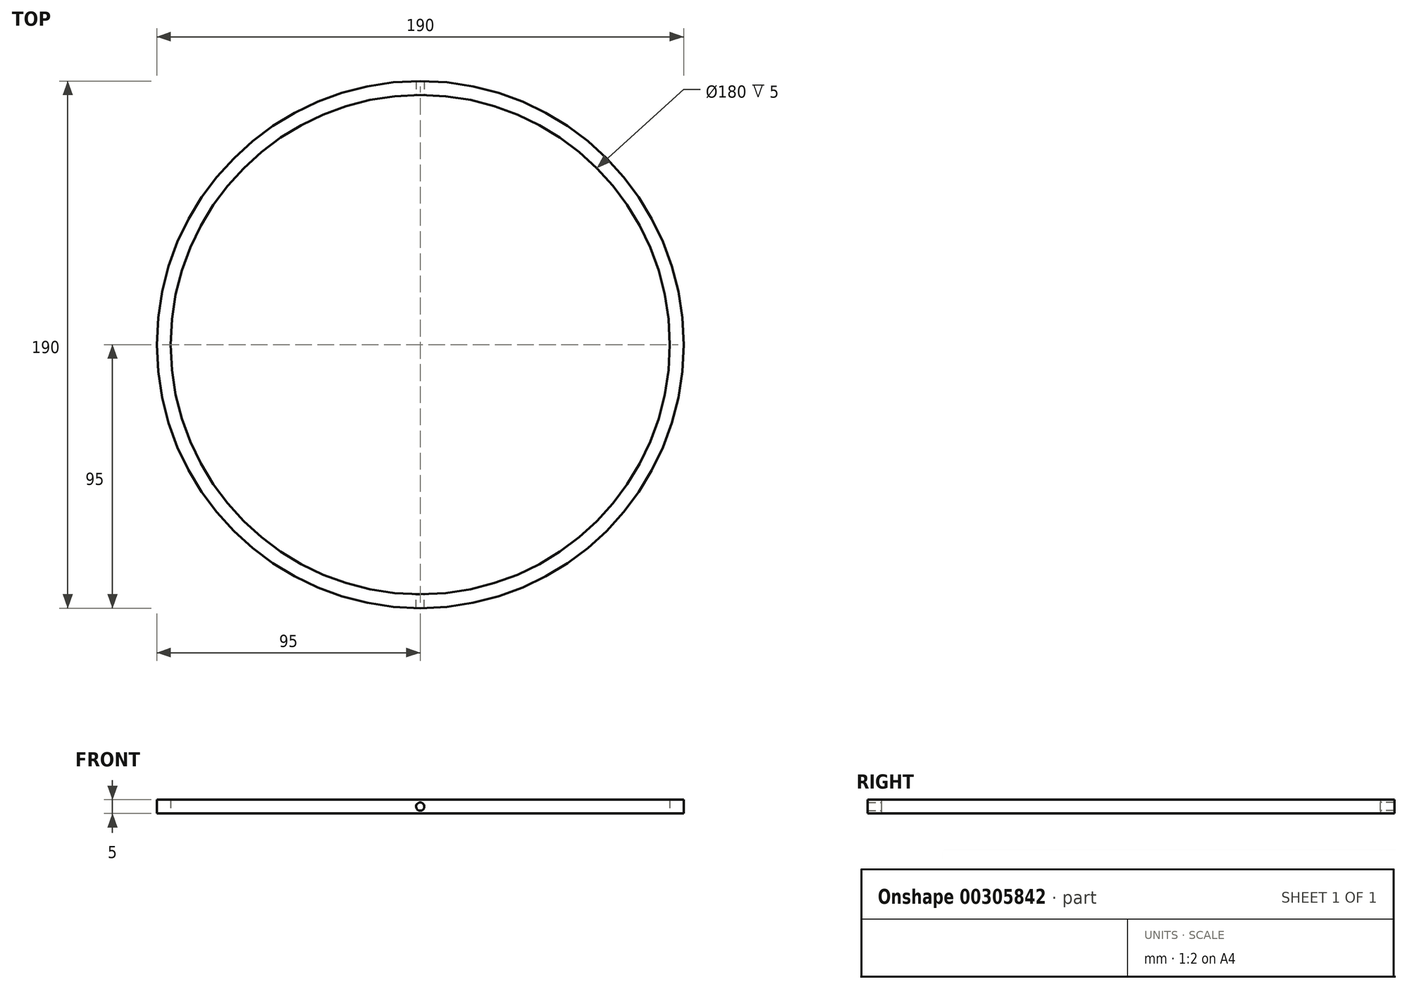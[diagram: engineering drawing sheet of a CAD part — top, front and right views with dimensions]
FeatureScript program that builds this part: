
annotation { "Feature Type Name" : "Feature", "Feature Type Description" : "" }
export const myFeature = defineFeature(function(context is Context, id is Id, definition is map)
    precondition{}
    {
        {
            var Q0;
            Q0=qCreatedBy(makeId("Front.planeOp"),FACE);
            var sketch = newSketch(context, id + "F0", { "sketchPlane" : qUnion([Q0])});
            skLineSegment(sketch, "E0.bottom", {"start": v(-95, 5) * mm, "end": v(-90, 5) * mm});
            skLineSegment(sketch, "E0.top", {"start": v(-95, 0) * mm, "end": v(-90, 0) * mm});
            skLineSegment(sketch, "E0.left", {"start": v(-95, 5) * mm, "end": v(-95, 0) * mm});
            skLineSegment(sketch, "E0.right", {"start": v(-90, 5) * mm, "end": v(-90, 0) * mm});
            skLineSegment(sketch, "E1", {"start": v(0, 0) * mm, "end": v(0, 2.5) * mm});
            skPoint(sketch, "E2", {"position": v(0, 2.5) * mm});
            skSolve(sketch);
        }
        {
            var Q0;
            Q0=makeQuery(id+"F0.imprint","IMPRINT",FACE,{"disambiguationData":[TD([[makeQuery(id+"F0.imprint","IMPRINT",EDGE,{"derivedFrom":sQuery(id+"F0.wireOp",EDGE,"E0.bottom")}),-1.0]])]});
            var Q1;
            Q1=sQuery(id+"F0.wireOp",EDGE,"E1");
            revolve(context, id + "F1", {"entities" : qUnion([Q0]), "axis" : qUnion([Q1]), "revolveType" : RevolveType.FULL});
        }
        {
            var Q0;
            Q0=sQuery(id+"F0.wireOp",VERTEX,"E2");
            var Q1;
            Q1=makeQuery(id+"F1.opRevolve","SWEPT_BODY",BODY,{"disambiguationData":[OSD([sQuery(id+"F0.wireOp",EDGE,"E0.bottom"),sQuery(id+"F0.wireOp",EDGE,"E0.top"),sQuery(id+"F0.wireOp",EDGE,"E0.left"),sQuery(id+"F0.wireOp",EDGE,"E0.right")])]});
            hole(context, id + "F2", {"style" : HoleStyle.SIMPLE, "endStyle" : HoleEndStyle.THROUGH, "holeDiameter" : 3 * mm, "tappedDepth" : 12 * mm, "tapClearance" : 3, "locations" : qUnion([Q0]), "scope" : qUnion([Q1])});
        }
        {
            var Q0;
            Q0=sQuery(id+"F0.wireOp",VERTEX,"E2");
            var Q1;
            Q1=makeQuery(id+"F1.opRevolve","SWEPT_BODY",BODY,{"disambiguationData":[OSD([sQuery(id+"F0.wireOp",EDGE,"E0.bottom"),sQuery(id+"F0.wireOp",EDGE,"E0.top"),sQuery(id+"F0.wireOp",EDGE,"E0.left"),sQuery(id+"F0.wireOp",EDGE,"E0.right")])]});
            hole(context, id + "F3", {"style" : HoleStyle.SIMPLE, "endStyle" : HoleEndStyle.THROUGH, "oppositeDirection" : true, "holeDiameter" : 3 * mm, "tappedDepth" : 12 * mm, "tapClearance" : 3, "locations" : qUnion([Q0]), "scope" : qUnion([Q1])});
        }
    });
